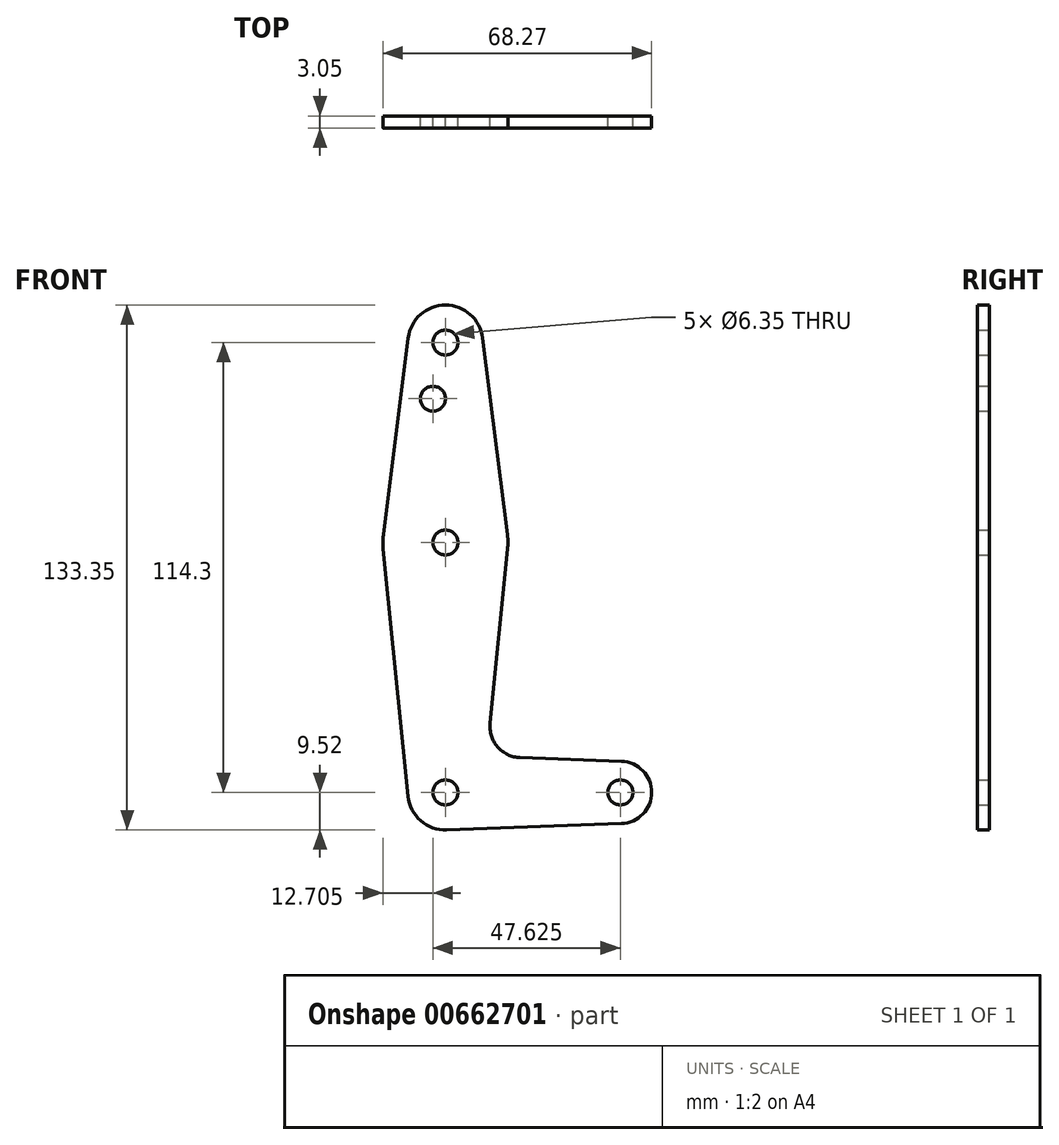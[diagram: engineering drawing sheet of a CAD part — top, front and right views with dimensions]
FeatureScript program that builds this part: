
annotation { "Feature Type Name" : "Feature", "Feature Type Description" : "" }
export const myFeature = defineFeature(function(context is Context, id is Id, definition is map)
    precondition{}
    {
        {
            var Q0;
            Q0=qCreatedBy(makeId("Front.planeOp"),FACE);
            var sketch = newSketch(context, id + "F0", { "sketchPlane" : qUnion([Q0])});
            skCircle(sketch, "E0", {"center": v(0, 0) * mm, "radius": 9.53 * mm});
            skCircle(sketch, "E1", {"center": v(0, 63.5) * mm, "radius": 15.88 * mm});
            skCircle(sketch, "E2", {"center": v(0, 114.3) * mm, "radius": 9.53 * mm});
            skCircle(sketch, "E3", {"center": v(44.45, 0) * mm, "radius": 7.94 * mm});
            skLineSegment(sketch, "E4", {"start": v(0, 63.5) * mm, "end": v(0, 0) * mm, "construction": true});
            skLineSegment(sketch, "E5", {"start": v(0, 0) * mm, "end": v(44.45, 0) * mm, "construction": true});
            skLineSegment(sketch, "E6", {"start": v(0, 63.5) * mm, "end": v(0, 114.3) * mm, "construction": true});
            skLineSegment(sketch, "E7", {"start": v(-9.45, 115.5) * mm, "end": v(-15.75, 65.48) * mm});
            skLineSegment(sketch, "E8", {"start": v(9.45, 115.5) * mm, "end": v(15.75, 65.48) * mm});
            skLineSegment(sketch, "E9", {"start": v(-15.8, 61.91) * mm, "end": v(-9.48, -0.95) * mm});
            skLineSegment(sketch, "E10", {"start": v(11.34, 17.6) * mm, "end": v(15.8, 61.91) * mm});
            skLineSegment(sketch, "E11", {"start": v(0.34, -9.52) * mm, "end": v(44.73, -7.93) * mm});
            skLineSegment(sketch, "E12", {"start": v(18.97, 8.85) * mm, "end": v(44.73, 7.93) * mm});
            skArc(sketch, "E13.filletArc", {"start": v(11.34, 17.6) * mm, "mid": v(13.26, 11.57) * mm, "end": v(18.97, 8.85) * mm});
            skCircle(sketch, "E14", {"center": v(0, 114.3) * mm, "radius": 3.18 * mm});
            skCircle(sketch, "E15", {"center": v(0, 63.5) * mm, "radius": 3.18 * mm});
            skCircle(sketch, "E16", {"center": v(-3.18, 100.03) * mm, "radius": 3.18 * mm});
            skCircle(sketch, "E17", {"center": v(0, 0) * mm, "radius": 3.18 * mm});
            skCircle(sketch, "E18", {"center": v(44.45, 0) * mm, "radius": 3.18 * mm});
            skSolve(sketch);
        }
        {
            var Q0;
            Q0=makeQuery(id+"F0.imprint","IMPRINT",FACE,{"disambiguationData":[TD([[makeQuery(id+"F0.imprint","IMPRINT",EDGE,{"derivedFrom":sQuery(id+"F0.wireOp",EDGE,"E17")}),-1.0]])]});
            var Q1;
            Q1=makeQuery(id+"F0.imprint","IMPRINT",FACE,{"disambiguationData":[TD([[makeQuery(id+"F0.imprint","IMPRINT",EDGE,{"derivedFrom":sQuery(id+"F0.wireOp",EDGE,"E14")}),-1.0]])]});
            var Q2;
            Q2=makeQuery(id+"F0.imprint","IMPRINT",FACE,{"disambiguationData":[TD([[makeQuery(id+"F0.imprint","IMPRINT",EDGE,{"derivedFrom":sQuery(id+"F0.wireOp",EDGE,"E18")}),-1.0]])]});
            var Q3;
            {var subQ0=sQuery(id+"F0.wireOp",EDGE,"E9");Q3=makeQuery(id+"F0.imprint","IMPRINT",FACE,{"disambiguationData":[TD([[makeQuery(id+"F0.imprint","IMPRINT",EDGE,{"derivedFrom":subQ0}),1.0]])]});}
            var Q4;
            Q4=makeQuery(id+"F0.imprint","IMPRINT",FACE,{"disambiguationData":[TD([[makeQuery(id+"F0.imprint","IMPRINT",EDGE,{"derivedFrom":sQuery(id+"F0.wireOp",EDGE,"E15")}),-1.0]])]});
            var Q5;
            {var subQ1=sQuery(id+"F0.wireOp",EDGE,"E7");Q5=makeQuery(id+"F0.imprint","IMPRINT",FACE,{"disambiguationData":[TD([[makeQuery(id+"F0.imprint","IMPRINT",EDGE,{"derivedFrom":subQ1}),1.0]])]});}
            extrude(context, id + "F1", {"entities" : qUnion([Q0, Q1, Q2, Q3, Q4, Q5]), "depth" : 3.05 * mm, "offsetDistance" : 25.4 * mm});
        }
    });
